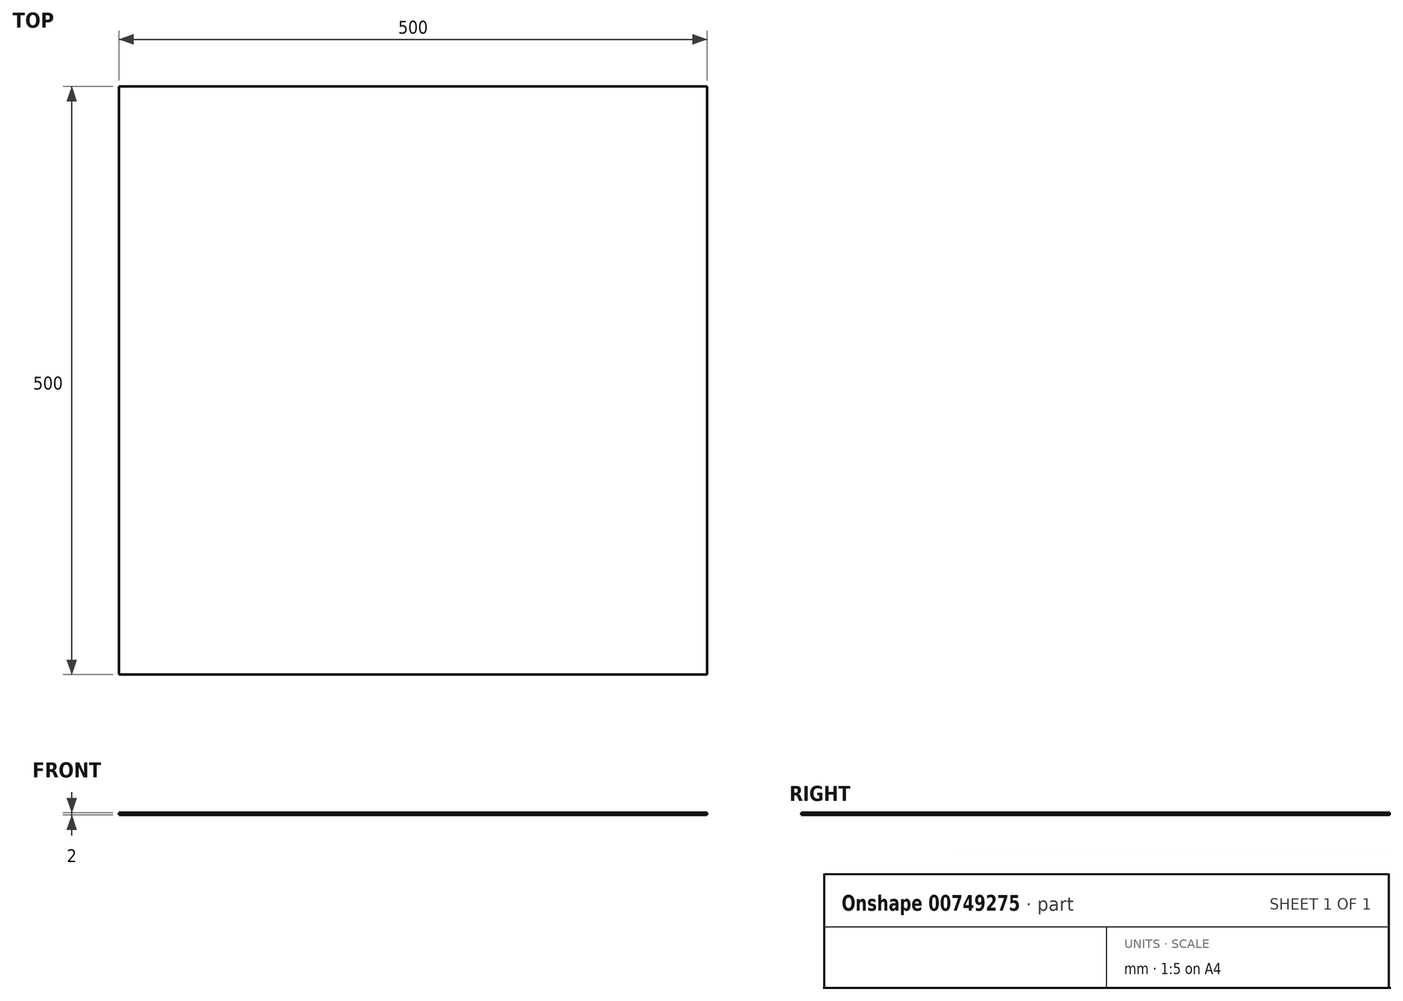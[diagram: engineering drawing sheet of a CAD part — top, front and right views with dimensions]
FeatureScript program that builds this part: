
annotation { "Feature Type Name" : "Feature", "Feature Type Description" : "" }
export const myFeature = defineFeature(function(context is Context, id is Id, definition is map)
    precondition{}
    {
        {
            assignVariable(context, id + "F0", {"name" : "glass_W", "anyValue" : 2});
        }
        {
            var Q0;
            Q0=qCreatedBy(makeId("Top.planeOp"),FACE);
            var sketch = newSketch(context, id + "F1", { "sketchPlane" : qUnion([Q0])});
            skLineSegment(sketch, "E0.bottom", {"start": v(-250, 250) * mm, "end": v(250, 250) * mm});
            skLineSegment(sketch, "E0.top", {"start": v(-250, -250) * mm, "end": v(250, -250) * mm});
            skLineSegment(sketch, "E0.left", {"start": v(-250, 250) * mm, "end": v(-250, -250) * mm});
            skLineSegment(sketch, "E0.right", {"start": v(250, 250) * mm, "end": v(250, -250) * mm});
            skPoint(sketch, "E0.middle", {"position": v(0, 0) * mm});
            skSolve(sketch);
        }
        {
            var Q0;
            Q0=makeQuery(id+"F1.imprint","IMPRINT",FACE,{"disambiguationData":[TD([[makeQuery(id+"F1.imprint","IMPRINT",EDGE,{"derivedFrom":sQuery(id+"F1.wireOp",EDGE,"E0.bottom")}),-1.0]])]});
            extrude(context, id + "F2", {"entities" : qUnion([Q0]), "depth" : (getVariable(context, 'glass_W')) * mm, "offsetDistance" : 25 * mm});
        }
    });
